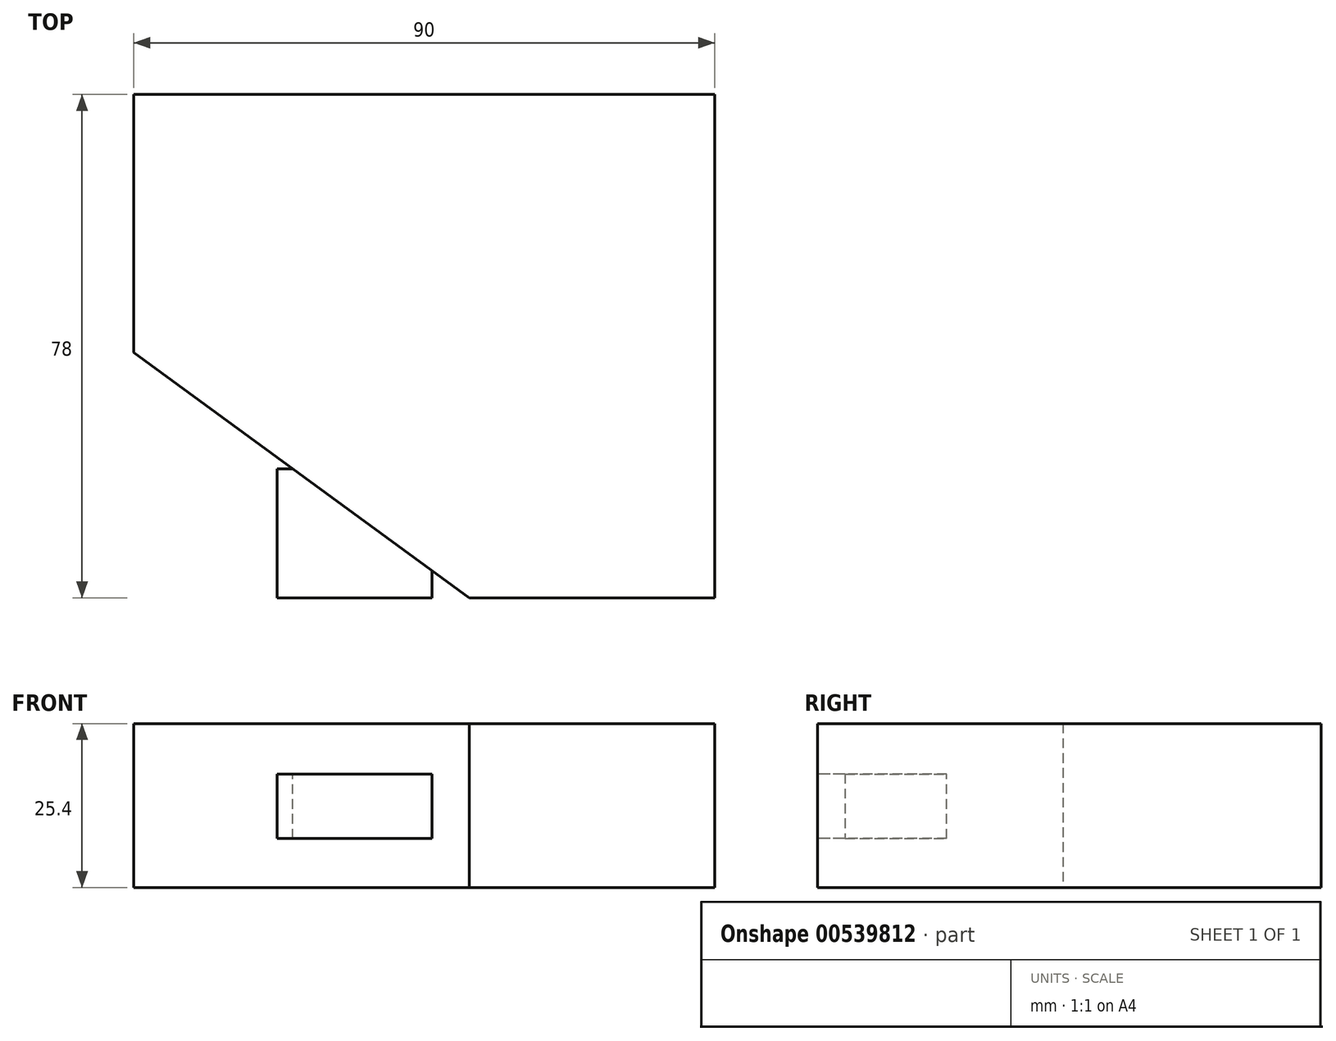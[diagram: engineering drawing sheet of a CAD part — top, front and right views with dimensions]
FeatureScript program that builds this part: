
annotation { "Feature Type Name" : "Feature", "Feature Type Description" : "" }
export const myFeature = defineFeature(function(context is Context, id is Id, definition is map)
    precondition{}
    {
        {
            var Q0;
            Q0=qCreatedBy(makeId("Top.planeOp"),FACE);
            var sketch = newSketch(context, id + "F0", { "sketchPlane" : qUnion([Q0])});
            skLineSegment(sketch, "E0", {"start": v(0, 0) * mm, "end": v(90, 0) * mm});
            skLineSegment(sketch, "E1", {"start": v(0, 0) * mm, "end": v(0, -40) * mm});
            skLineSegment(sketch, "E2", {"start": v(90, 0) * mm, "end": v(90, -78) * mm});
            skLineSegment(sketch, "E3", {"start": v(90, -78) * mm, "end": v(52, -78) * mm});
            skLineSegment(sketch, "E4", {"start": v(52, -78) * mm, "end": v(0, -40) * mm});
            skSolve(sketch);
        }
        {
            var Q0;
            Q0=makeQuery(id+"F0.imprint","IMPRINT",FACE,{"disambiguationData":[TD([[makeQuery(id+"F0.imprint","IMPRINT",EDGE,{"derivedFrom":sQuery(id+"F0.wireOp",EDGE,"E0")}),-1.0]])]});
            extrude(context, id + "F1", {"entities" : qUnion([Q0]), "depth" : 25.4 * mm, "offsetDistance" : 25.4 * mm});
        }
        {
            var Q0;
            Q0=makeQuery(id+"F1.opExtrude","SWEPT_FACE",FACE,{"disambiguationData":[OSD([sQuery(id+"F0.wireOp",EDGE,"E3")])]});
            var sketch = newSketch(context, id + "F2", { "sketchPlane" : qUnion([Q0])});
            skLineSegment(sketch, "E5.bottom", {"start": v(46.22, 17.59) * mm, "end": v(22.22, 17.59) * mm});
            skLineSegment(sketch, "E5.top", {"start": v(46.22, 7.59) * mm, "end": v(22.22, 7.59) * mm});
            skLineSegment(sketch, "E5.left", {"start": v(46.22, 17.59) * mm, "end": v(46.22, 7.59) * mm});
            skLineSegment(sketch, "E5.right", {"start": v(22.22, 17.59) * mm, "end": v(22.22, 7.59) * mm});
            skSolve(sketch);
        }
        {
            var Q0;
            Q0=makeQuery(id+"F2.imprint","IMPRINT",FACE,{"disambiguationData":[TD([[makeQuery(id+"F2.imprint","IMPRINT",EDGE,{"derivedFrom":sQuery(id+"F2.wireOp",EDGE,"E5.bottom")}),1.0]])]});
            extrude(context, id + "F3", {"entities" : qUnion([Q0]), "operationType" : NewBodyOperationType.ADD, "oppositeDirection" : true, "depth" : 20 * mm, "offsetDistance" : 25 * mm});
        }
    });
